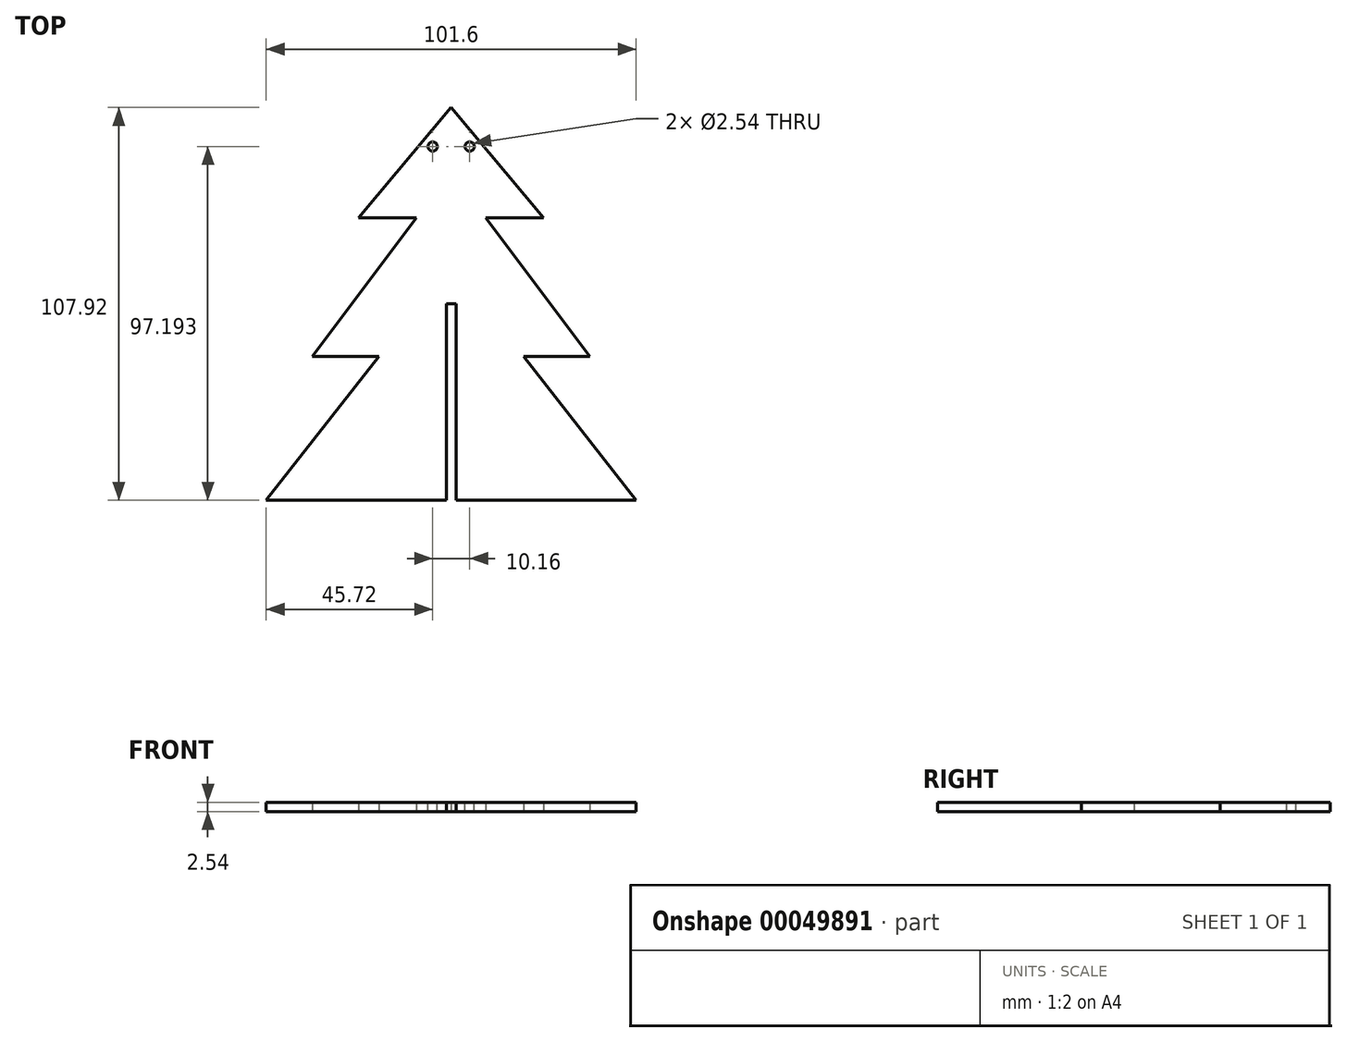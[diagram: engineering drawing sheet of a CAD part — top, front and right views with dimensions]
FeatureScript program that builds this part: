
annotation { "Feature Type Name" : "Feature", "Feature Type Description" : "" }
export const myFeature = defineFeature(function(context is Context, id is Id, definition is map)
    precondition{}
    {
        {
            var Q0;
            Q0=qCreatedBy(makeId("Top.planeOp"),FACE);
            var sketch = newSketch(context, id + "F0", { "sketchPlane" : qUnion([Q0])});
            skLineSegment(sketch, "E0", {"start": v(0, 68.38) * mm, "end": v(-25.4, 38.1) * mm});
            skLineSegment(sketch, "E1", {"start": v(-25.4, 38.1) * mm, "end": v(25.4, 38.1) * mm});
            skLineSegment(sketch, "E2", {"start": v(25.4, 38.1) * mm, "end": v(0, 68.38) * mm});
            skLineSegment(sketch, "E3", {"start": v(0, 50.8) * mm, "end": v(-38.1, 0) * mm});
            skLineSegment(sketch, "E4", {"start": v(-38.1, 0) * mm, "end": v(38.1, 0) * mm});
            skLineSegment(sketch, "E5", {"start": v(38.1, 0) * mm, "end": v(0, 50.8) * mm});
            skLineSegment(sketch, "E6", {"start": v(0, 25.4) * mm, "end": v(-50.8, -39.54) * mm});
            skLineSegment(sketch, "E7", {"start": v(-50.8, -39.54) * mm, "end": v(50.8, -39.54) * mm});
            skLineSegment(sketch, "E8", {"start": v(50.8, -39.54) * mm, "end": v(0, 25.4) * mm});
            skLineSegment(sketch, "E9.bottom", {"start": v(-1.27, -39.54) * mm, "end": v(1.33, -39.54) * mm});
            skLineSegment(sketch, "E9.top", {"start": v(-1.27, 14.42) * mm, "end": v(1.33, 14.42) * mm});
            skLineSegment(sketch, "E9.left", {"start": v(-1.27, -39.54) * mm, "end": v(-1.27, 14.42) * mm});
            skLineSegment(sketch, "E9.right", {"start": v(1.33, -39.54) * mm, "end": v(1.33, 14.42) * mm});
            skSolve(sketch);
        }
        {
            var Q0;
            {var subQ0=sQuery(id+"F0.wireOp",EDGE,"E6");var subQ1=sQuery(id+"F0.wireOp",EDGE,"E4");var subQ2=makeQuery(id+"F0.imprint","INTERSECT",VERTEX,{"derivedFrom":[subQ1,subQ0]});Q0=makeQuery(id+"F0.imprint","IMPRINT",FACE,{"disambiguationData":[TD([[makeQuery(id+"F0.imprint","IMPRINT",EDGE,{"disambiguationData":[TD([[subQ2,-1.0]])],"derivedFrom":subQ1}),-1.0]])]});}
            var Q1;
            {var subQ0=sQuery(id+"F0.wireOp",EDGE,"E8");var subQ1=sQuery(id+"F0.wireOp",EDGE,"E4");var subQ2=makeQuery(id+"F0.imprint","INTERSECT",VERTEX,{"derivedFrom":[subQ1,subQ0]});Q1=makeQuery(id+"F0.imprint","IMPRINT",FACE,{"disambiguationData":[TD([[makeQuery(id+"F0.imprint","IMPRINT",EDGE,{"disambiguationData":[TD([[subQ2,1.0]])],"derivedFrom":subQ1}),-1.0]])]});}
            var Q2;
            {var subQ7=sQuery(id+"F0.wireOp",EDGE,"E9.top");Q2=makeQuery(id+"F0.imprint","IMPRINT",FACE,{"disambiguationData":[TD([[makeQuery(id+"F0.imprint","IMPRINT",EDGE,{"derivedFrom":subQ7}),1.0]])]});}
            var Q3;
            {var subQ5=sQuery(id+"F0.wireOp",EDGE,"E3");var subQ10=sQuery(id+"F0.wireOp",EDGE,"E1");var subQ11=makeQuery(id+"F0.imprint","INTERSECT",VERTEX,{"derivedFrom":[subQ10,subQ5]});Q3=makeQuery(id+"F0.imprint","IMPRINT",FACE,{"disambiguationData":[TD([[makeQuery(id+"F0.imprint","IMPRINT",EDGE,{"disambiguationData":[TD([[subQ11,-1.0]])],"derivedFrom":subQ10}),-1.0]])]});}
            var Q4;
            {var subQ0=sQuery(id+"F0.wireOp",EDGE,"E3");var subQ1=sQuery(id+"F0.wireOp",EDGE,"E1");var subQ2=makeQuery(id+"F0.imprint","INTERSECT",VERTEX,{"derivedFrom":[subQ1,subQ0]});Q4=makeQuery(id+"F0.imprint","IMPRINT",FACE,{"disambiguationData":[TD([[makeQuery(id+"F0.imprint","IMPRINT",EDGE,{"disambiguationData":[TD([[subQ2,-1.0]])],"derivedFrom":subQ1}),1.0]])]});}
            var Q5;
            {var subQ4=sQuery(id+"F0.wireOp",EDGE,"E0");Q5=makeQuery(id+"F0.imprint","IMPRINT",FACE,{"disambiguationData":[TD([[makeQuery(id+"F0.imprint","IMPRINT",EDGE,{"derivedFrom":subQ4}),1.0]])]});}
            extrude(context, id + "F1", {"entities" : qUnion([Q0, Q1, Q2, Q3, Q4, Q5]), "depth" : 2.54 * mm});
        }
        {
            var Q0;
            Q0=makeQuery(id+"F1.opExtrude","CAP_FACE",FACE,{"disambiguationData":[OSD([sQuery(id+"F0.wireOp",EDGE,"E0"),sQuery(id+"F0.wireOp",EDGE,"E1"),sQuery(id+"F0.wireOp",EDGE,"E2"),sQuery(id+"F0.wireOp",EDGE,"E3"),sQuery(id+"F0.wireOp",EDGE,"E4"),sQuery(id+"F0.wireOp",EDGE,"E5"),sQuery(id+"F0.wireOp",EDGE,"E6"),sQuery(id+"F0.wireOp",EDGE,"E7"),sQuery(id+"F0.wireOp",EDGE,"E8"),sQuery(id+"F0.wireOp",EDGE,"E9.top"),sQuery(id+"F0.wireOp",EDGE,"E9.left"),sQuery(id+"F0.wireOp",EDGE,"E9.right")])],"isStart":false});
            var sketch = newSketch(context, id + "F2", { "sketchPlane" : qUnion([Q0])});
            skCircle(sketch, "E10", {"center": v(-5.08, 57.65) * mm, "radius": 1.27 * mm});
            skCircle(sketch, "E11.MirrorC", {"center": v(5.08, 57.65) * mm, "radius": 1.27 * mm});
            skSolve(sketch);
        }
        {
            var Q0;
            Q0=sQuery(id+"F2.wireOp",VERTEX,"E10.center");
            var Q1;
            Q1=sQuery(id+"F2.wireOp",VERTEX,"E11.MirrorC.center");
            var Q2;
            Q2=makeQuery(id+"F1.opExtrude","SWEPT_BODY",BODY,{"disambiguationData":[OSD([sQuery(id+"F0.wireOp",EDGE,"E0"),sQuery(id+"F0.wireOp",EDGE,"E1"),sQuery(id+"F0.wireOp",EDGE,"E2"),sQuery(id+"F0.wireOp",EDGE,"E3"),sQuery(id+"F0.wireOp",EDGE,"E4"),sQuery(id+"F0.wireOp",EDGE,"E5"),sQuery(id+"F0.wireOp",EDGE,"E6"),sQuery(id+"F0.wireOp",EDGE,"E7"),sQuery(id+"F0.wireOp",EDGE,"E8"),sQuery(id+"F0.wireOp",EDGE,"E9.top"),sQuery(id+"F0.wireOp",EDGE,"E9.left"),sQuery(id+"F0.wireOp",EDGE,"E9.right")])]});
            hole(context, id + "F3", {"style" : HoleStyle.SIMPLE, "holeDiameter" : 2.54 * mm, "endStyle" : HoleEndStyle.THROUGH, "locations" : qUnion([Q0, Q1]), "scope" : qUnion([Q2])});
        }
    });
